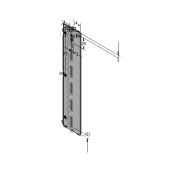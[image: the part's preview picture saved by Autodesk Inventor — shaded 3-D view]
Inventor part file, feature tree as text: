
AUTODESK INVENTOR PART (.ipt)
format: ipt  version: 2022 (Build 260153000, 153)  size: 192,000 bytes
history: native  units: mm
features: extrude x2, sketch x1
ambient origin geometry x8: Origin, YZ Plane, XZ Plane, XY Plane, X Axis, Y Axis, Z Axis, Center Point
bodies: Solid1 (feature_tree)
feature tree (3):
  sketch  "Sketch1"  dims[d0=35.0mm d1=180.0mm d2=3.0mm d3=20.0mm d4=5.0mm d5=14.0mm d6=60.0mm d8=30.0mm d9=10.0mm d11=10.0mm d13=5.0mm d14=4.15mm d15=4.0mm d16=10.0mm d17=30.0mm d19=75.0mm d20=10.0mm d22=10.0mm d24=5.0mm d25=45.0deg d26=7.071068mm d27=7.071068mm d28=20.0mm d29=180.0mm d31=10.0mm d32=10.0mm d34=10.0mm d36=2.0mm d37=0.0mm d38=2.5mm d39=0.0mm]
  extrude  "Extrusion1"  Depth=180.0mm
  extrude  "Extrusion2"  Depth=3.0mm
